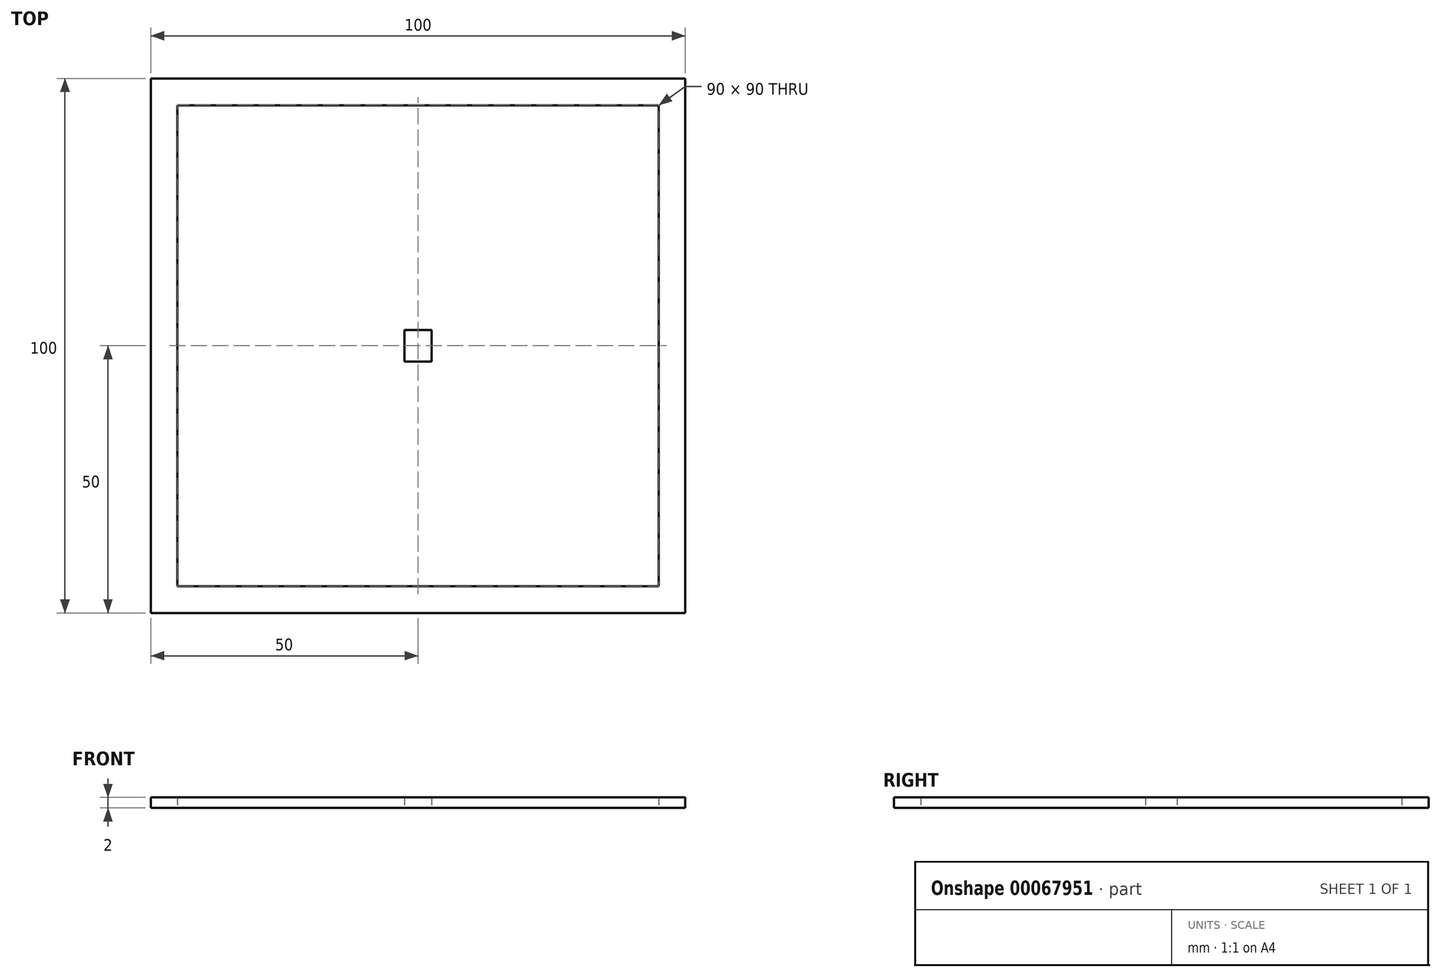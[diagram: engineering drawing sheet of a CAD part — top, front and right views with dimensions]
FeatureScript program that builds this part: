
annotation { "Feature Type Name" : "Feature", "Feature Type Description" : "" }
export const myFeature = defineFeature(function(context is Context, id is Id, definition is map)
    precondition{}
    {
        {
            var Q0;
            Q0=qCreatedBy(makeId("Top.planeOp"),FACE);
            var sketch = newSketch(context, id + "F0", { "sketchPlane" : qUnion([Q0])});
            skLineSegment(sketch, "E0.rect.bottom", {"start": v(50, 50) * mm, "end": v(-50, 50) * mm});
            skLineSegment(sketch, "E0.rect.top", {"start": v(50, -50) * mm, "end": v(-50, -50) * mm});
            skLineSegment(sketch, "E0.rect.left", {"start": v(50, 50) * mm, "end": v(50, -50) * mm});
            skLineSegment(sketch, "E0.rect.right", {"start": v(-50, 50) * mm, "end": v(-50, -50) * mm});
            skPoint(sketch, "E0.rect.middle", {"position": v(0, 0) * mm});
            skLineSegment(sketch, "E1.rect.bottom", {"start": v(45, 45) * mm, "end": v(-45, 45) * mm});
            skLineSegment(sketch, "E1.rect.top", {"start": v(45, -45) * mm, "end": v(-45, -45) * mm});
            skLineSegment(sketch, "E1.rect.left", {"start": v(45, 45) * mm, "end": v(45, -45) * mm});
            skLineSegment(sketch, "E1.rect.right", {"start": v(-45, 45) * mm, "end": v(-45, -45) * mm});
            skLineSegment(sketch, "E2.rect.bottom", {"start": v(2.53, -45) * mm, "end": v(-2.53, -45) * mm});
            skLineSegment(sketch, "E2.rect.top", {"start": v(2.53, 45) * mm, "end": v(-2.53, 45) * mm});
            skLineSegment(sketch, "E2.rect.left", {"start": v(2.53, -45) * mm, "end": v(2.53, 45) * mm});
            skLineSegment(sketch, "E2.rect.right", {"start": v(-2.53, -45) * mm, "end": v(-2.53, 45) * mm});
            skLineSegment(sketch, "E3.rect.bottom", {"start": v(45, -2.96) * mm, "end": v(-45, -2.96) * mm});
            skLineSegment(sketch, "E3.rect.top", {"start": v(45, 2.96) * mm, "end": v(-45, 2.96) * mm});
            skLineSegment(sketch, "E3.rect.left", {"start": v(45, -2.96) * mm, "end": v(45, 2.96) * mm});
            skLineSegment(sketch, "E3.rect.right", {"start": v(-45, -2.96) * mm, "end": v(-45, 2.96) * mm});
            skSolve(sketch);
        }
        {
            var Q0;
            {var subQ0=sQuery(id+"F0.wireOp",EDGE,"E2.rect.top");Q0=makeQuery(id+"F0.imprint","IMPRINT",FACE,{"disambiguationData":[TD([[makeQuery(id+"F0.imprint","IMPRINT",EDGE,{"derivedFrom":subQ0}),1.0]])]});}
            var Q1;
            Q1=makeQuery(id+"F0.imprint","IMPRINT",FACE,{"disambiguationData":[TD([[makeQuery(id+"F0.imprint","IMPRINT",EDGE,{"derivedFrom":sQuery(id+"F0.wireOp",EDGE,"E0.rect.bottom")}),1.0]])]});
            var Q2;
            {var subQ5=sQuery(id+"F0.wireOp",EDGE,"E3.rect.right");Q2=makeQuery(id+"F0.imprint","IMPRINT",FACE,{"disambiguationData":[TD([[makeQuery(id+"F0.imprint","IMPRINT",EDGE,{"derivedFrom":subQ5}),-1.0]])]});}
            var Q3;
            {var subQ5=sQuery(id+"F0.wireOp",EDGE,"E3.rect.left");Q3=makeQuery(id+"F0.imprint","IMPRINT",FACE,{"disambiguationData":[TD([[makeQuery(id+"F0.imprint","IMPRINT",EDGE,{"derivedFrom":subQ5}),1.0]])]});}
            var Q4;
            {var subQ0=sQuery(id+"F0.wireOp",EDGE,"E2.rect.bottom");Q4=makeQuery(id+"F0.imprint","IMPRINT",FACE,{"disambiguationData":[TD([[makeQuery(id+"F0.imprint","IMPRINT",EDGE,{"derivedFrom":subQ0}),-1.0]])]});}
            var Q5;
            {var subQ0=sQuery(id+"F0.wireOp",EDGE,"E3.rect.bottom");var subQ1=sQuery(id+"F0.wireOp",EDGE,"E2.rect.left");var subQ2=makeQuery(id+"F0.imprint","INTERSECT",VERTEX,{"derivedFrom":[subQ1,subQ0]});Q5=makeQuery(id+"F0.imprint","IMPRINT",FACE,{"disambiguationData":[TD([[makeQuery(id+"F0.imprint","IMPRINT",EDGE,{"disambiguationData":[TD([[subQ2,-1.0]])],"derivedFrom":subQ1}),1.0]])]});}
            extrude(context, id + "F1", {"entities" : qUnion([Q0, Q1, Q2, Q3, Q4, Q5]), "depth" : 2 * mm});
        }
    });
